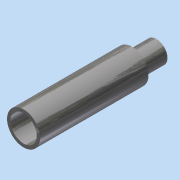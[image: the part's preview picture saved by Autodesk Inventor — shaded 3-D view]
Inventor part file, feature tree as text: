
AUTODESK INVENTOR PART (.ipt)
format: ipt  version: 2015 (Build 190159000, 159)  size: 100,864 bytes
history: native  units: in
note: dims shown in document units (in); Inventor stores cm internally (conversion verified against a paired STEP export)
features: extrude x3, sketch x3
ambient origin geometry x8: Origin, YZ Plane, XZ Plane, XY Plane, X Axis, Y Axis, Z Axis, Center Point
bodies: Solid1 (feature_tree)
feature tree (6):
  extrude  "Extrusion1"  Depth=0.5906in
  extrude  "Extrusion2"  Depth=1.9405in
  extrude  "Extrusion3"  Depth=0.4375in TaperAngle=0.0deg
  sketch  "Sketch1"  dims[d0=0.4724in d1=0.5906in]
  sketch  "Sketch2"  dims[d2=1.9405in d3=0.0in d4=0.3228in]
  sketch  "Sketch3"  dims[d5=0.3937in d6=0.4375in d7=0.0in d8=0.125in d9=0.0in]
